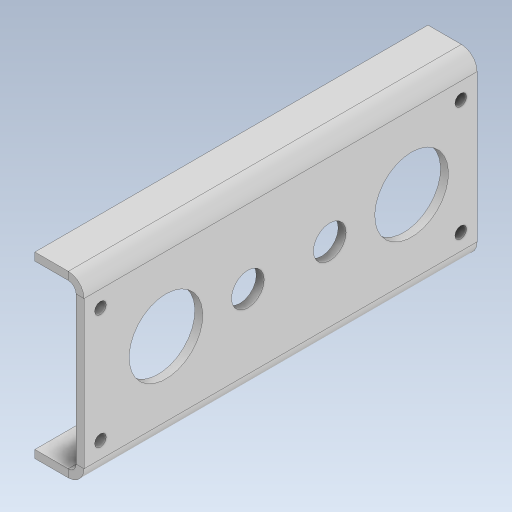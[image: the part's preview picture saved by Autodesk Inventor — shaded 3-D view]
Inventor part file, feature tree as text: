
AUTODESK INVENTOR PART (.ipt)
format: ipt  version: 2023 (Build 270158000, 158)  size: 172,032 bytes
history: native  units: in
note: dims shown in document units (in); Inventor stores cm internally (conversion verified against a paired STEP export)
features: sheet_metal_op x4, sketch x2, other x2
ambient origin geometry x8: Origin, YZ Plane, XZ Plane, XY Plane, X Axis, Y Axis, Z Axis, Center Point
bodies: Body1 (feature_tree)
feature tree (8):
  sheet_metal_op  "Face2"
  sheet_metal_op  "Flange1"
  sketch  "Sketch1"  dims[d0=2.25in]
  other  "Plate2"
  sketch  "Sketch2"  dims[d1=6.0in d2=1.25in d3=1.25in d4=1.25in d5=1.0in d6=1.125in d7=0.5in d8=1.125in d10=0.12in d11=0.177in d12=5.5in d13=1.75in d14=0.5in d15=6.0in d16=0.5in d17=6.0in d18=0.12in d19=0.06in d20=0.24in d21=0.12in d22=0.75in d23=90.0deg d24=0.12in d25=0.48in d26=0.12in d27=0.12in]
  other  "Plate3"
  sheet_metal_op  "Bend1"
  sheet_metal_op  "Corner1"
